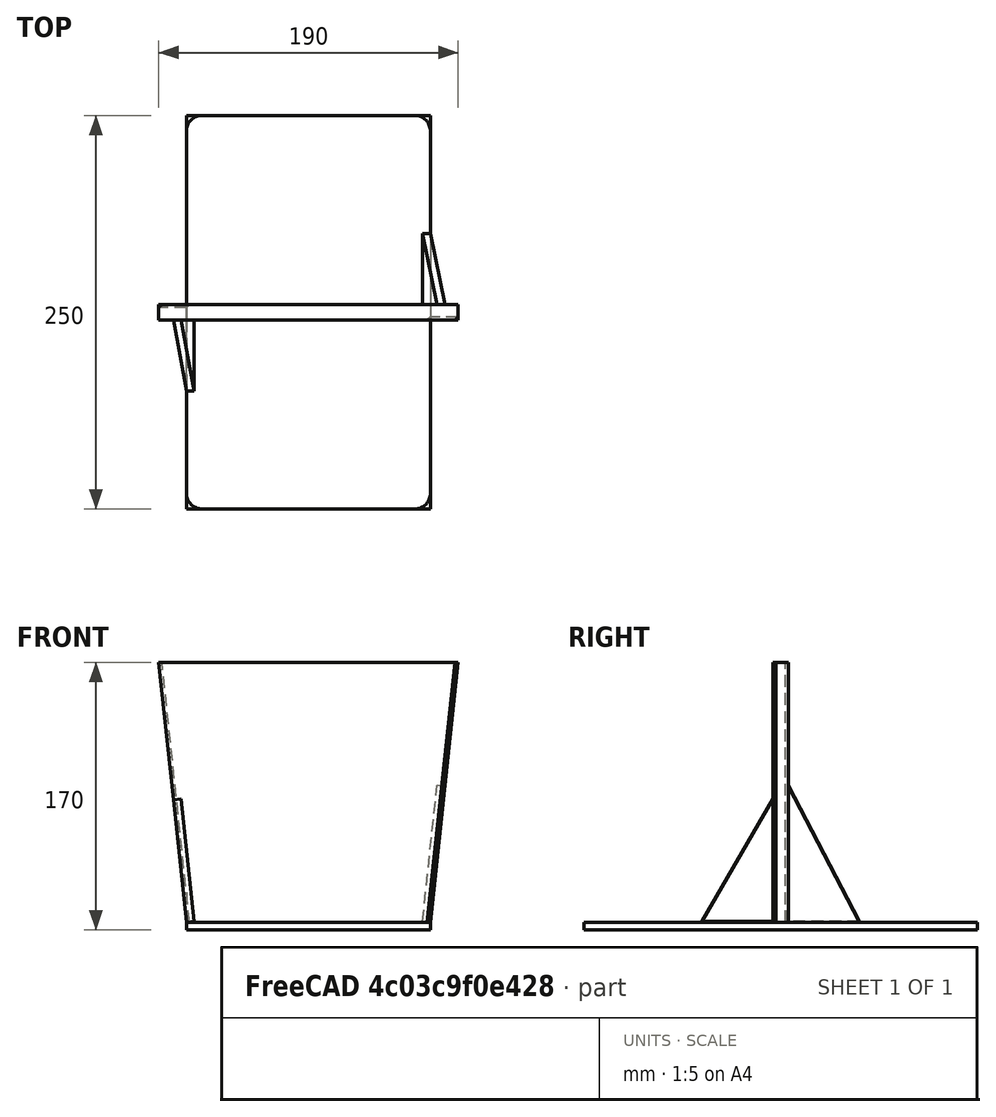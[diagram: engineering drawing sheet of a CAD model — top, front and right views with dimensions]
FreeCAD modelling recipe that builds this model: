
FCSTD DOCUMENT  (FreeCAD 0.16R)
Label: SockDivider
License: All rights reserved
LicenseURL: http://en.wikipedia.org/wiki/All_rights_reserved
objects: Sketcher::SketchObject×5, PartDesign::Pad×4, PartDesign::Pocket×1, PartDesign::Mirrored×1, PartDesign::Fillet×1, PartDesign::Chamfer×1, Mesh::Feature×1
note: 18 computed .brp shape members not serialized (recipe doc carries the construction recipe); baked Part::Feature solids carry a one-line shape summary decoded from their .brp

FEATURE [Sketcher::SketchObject] Sketch
  sketch-geometry (4):
    g0: LineSegment StartX=-77.5 StartY=125 StartZ=0 EndX=77.5 EndY=125 EndZ=0
    g1: LineSegment StartX=77.5 StartY=125 StartZ=0 EndX=77.5 EndY=-125 EndZ=0
    g2: LineSegment StartX=77.5 StartY=-125 StartZ=0 EndX=-77.5 EndY=-125 EndZ=0
    g3: LineSegment StartX=-77.5 StartY=-125 StartZ=0 EndX=-77.5 EndY=125 EndZ=0
  constraints (11):
    c: Coincident(g0,g1)
    c: Coincident(g1,g2)
    c: Coincident(g2,g3)
    c: Coincident(g3,g0)
    c: Horizontal(g0)
    c: Horizontal(g2)
    c: Vertical(g1)
    c: Vertical(g3)
    c: Distance(g0) = 155
    c: Distance(g1) = 250
    c: Symmetric(g0,g2,g-1)
FEATURE [PartDesign::Pad] Pad
  Length = 5
  Length2 = 100
  Sketch = -> Sketch
  Type = 0
FEATURE [Sketcher::SketchObject] Sketch001
  ExternalGeometry = -> [Pad]
  Placement = pos=(0,0,5) rot=(0,0,1;0rad)
  Support = -> Pad [Face6]
  sketch-geometry (4):
    g0: LineSegment StartX=-95 StartY=5 StartZ=0 EndX=95 EndY=5 EndZ=0
    g1: LineSegment StartX=95 StartY=5 StartZ=0 EndX=95 EndY=-5 EndZ=0
    g2: LineSegment StartX=95 StartY=-5 StartZ=0 EndX=-95 EndY=-5 EndZ=0
    g3: LineSegment StartX=-95 StartY=-5 StartZ=0 EndX=-95 EndY=5 EndZ=0
  constraints (12):
    c: Coincident(g0,g1)
    c: Coincident(g1,g2)
    c: Coincident(g2,g3)
    c: Coincident(g3,g0)
    c: Horizontal(g0)
    c: Horizontal(g2)
    c: Vertical(g1)
    c: Vertical(g3)
    c: Distance(g1) = 10
    c: Symmetric(g0,g1,g-1)
    c: Distance(g0) = 190
    c: Symmetric(g0,g0,g-2)
FEATURE [PartDesign::Pad] Pad001
  Length = 165
  Length2 = 100
  Sketch = -> Sketch001
  Type = 0
FEATURE [Sketcher::SketchObject] Sketch002
  ExternalGeometry = -> [Pad001]
  Placement = pos=(0,5,0) rot=(0,0.707107,0.707107;3.14159rad)
  Support = -> Pad001 [Face10]
  sketch-geometry (5):
    g0: LineSegment StartX=77.5 StartY=5 StartZ=0 EndX=95 EndY=170 EndZ=0
    g1: LineSegment StartX=95 StartY=170 StartZ=0 EndX=130.37 EndY=170 EndZ=0
    g2: LineSegment StartX=130.37 StartY=170 StartZ=0 EndX=130.37 EndY=-28.5457 EndZ=0
    g3: LineSegment StartX=130.37 StartY=-28.5457 StartZ=0 EndX=77.5 EndY=-28.5457 EndZ=0
    g4: LineSegment StartX=77.5 StartY=-28.5457 StartZ=0 EndX=77.5 EndY=5 EndZ=0
  constraints (11):
    c: Coincident(g-5,g0)
    c: Coincident(g0,g-3)
    c: Coincident(g0,g1)
    c: Horizontal(g1)
    c: Coincident(g1,g2)
    c: Vertical(g2)
    c: Coincident(g2,g3)
    c: Coincident(g3,g4)
    c: Coincident(g4,g0)
    c: Vertical(g4)
    c: Horizontal(g3)
FEATURE [PartDesign::Pocket] Pocket
  Length = 5
  Sketch = -> Sketch002
  Type = 1
FEATURE [PartDesign::Mirrored] Mirrored
  MirrorPlane = -> Sketch002 [V_Axis]
  Originals = -> [Pocket]
FEATURE [Sketcher::SketchObject] Sketch003
  ExternalGeometry = -> [Mirrored]
  Placement = pos=(-76.1135,0,-8.07264) rot=(0.596636,-0.596636,-0.536703;2.15644rad)
  Support = -> Mirrored [Face10]
  sketch-geometry (3):
    g0: LineSegment StartX=0 StartY=100 StartZ=0 EndX=50 EndY=13.146 EndZ=0
    g1: LineSegment StartX=50 StartY=13.146 StartZ=0 EndX=5 EndY=13.146 EndZ=0
    g2: LineSegment StartX=5 StartY=13.146 StartZ=0 EndX=0 EndY=100 EndZ=0
  constraints (8):
    c: PointOnObject(g0,g-2)
    c: PointOnObject(g0,g-3)
    c: Coincident(g0,g1)
    c: Coincident(g1,g-3)
    c: Coincident(g1,g2)
    c: Coincident(g2,g0)
    c: DistanceY(g0) = 100
    c: DistanceX(g0) = 50
FEATURE [PartDesign::Pad] Pad002
  Length = 5
  Length2 = 100
  Reversed = true
  Sketch = -> Sketch003
  Type = 0
FEATURE [Sketcher::SketchObject] Sketch004
  ExternalGeometry = -> [Pad002]
  Placement = pos=(76.1135,0,-8.07264) rot=(0.596636,0.596636,0.536703;2.15644rad)
  Support = -> Pad002 [Face12]
  sketch-geometry (3):
    g0: LineSegment StartX=5 StartY=100 StartZ=0 EndX=50 EndY=13.146 EndZ=0
    g1: LineSegment StartX=50 StartY=13.146 StartZ=0 EndX=5 EndY=13.146 EndZ=0
    g2: LineSegment StartX=5 StartY=13.146 StartZ=0 EndX=5 EndY=100 EndZ=0
  constraints (8):
    c: PointOnObject(g0,g-4)
    c: PointOnObject(g0,g-3)
    c: Coincident(g0,g1)
    c: Coincident(g1,g-4)
    c: Coincident(g1,g2)
    c: Coincident(g2,g0)
    c: DistanceY(g0) = 100
    c: DistanceX(g0) = 50
FEATURE [PartDesign::Pad] Pad003
  Length = 5
  Length2 = 100
  Reversed = true
  Sketch = -> Sketch004
  Type = 0
FEATURE [PartDesign::Fillet] Fillet
  Base = -> Pad003 [Edge17,Edge21,Edge2,Edge1]
  Radius = 10
FEATURE [PartDesign::Chamfer] Chamfer
  Base = -> Fillet [Edge56,Edge41]
  Size = 2
FEATURE [Mesh::Feature] Mesh  label="Chamfer (Meshed)"
